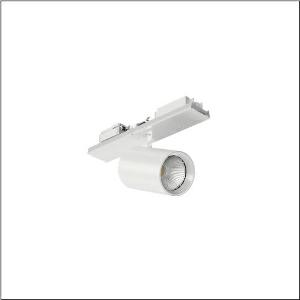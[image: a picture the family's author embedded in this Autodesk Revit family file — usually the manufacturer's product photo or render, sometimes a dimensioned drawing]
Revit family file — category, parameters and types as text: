
# Revit family: licross_r__spot_31_51sl13da45b_aeee
name_source: partatom
category: Lighting Fixtures
units: mm (PartAtom-declared; Revit-internal decimal feet)

## family parameters
Cut with Voids When Loaded = No
Host = Face
Light Source = No
Part Type = Normal
Room Calculation Point = No
Round Connector Dimension = Use Diameter
Shared = No

## types (1)
- --- (1 x LED, 5190 lm, 43.9 W, 4000K)
    Apparent Load = 44 VA
    CIE Flux Codes = 92 97 99 100 100
    Color Rendering = 90
    Color Temperature = 4000K
    Default Elevation = 1800 mm
    Description = Licross® Spot 31, directional spotlight, light control with lens, of plastic, LED rated luminous flux: 5.190lm, light colour: 940, with plug, 5-pole, mains connection: 220..240V, AC, 50/60Hz, of aluminium, traffic white (RAL 9016), length: 140mm, diameter: 90mm, protection rating (complete): IP20, insulation class (complete): insulation class I (protective earthing), certification: CE, packaging unit: 1 piece
    Height = 175 mm
    Lamp = 1 x LED
    Lamp Light Flux = 5190 lm
    Lamp Power = 43.9 W
    Lamp count = 1
    Length = 90 mm
    Luminous efficacy = 118 lm/W
    Manufacturer = Siteco
    ModVariant = No
    Model = 51SL13DA45B
    Mounting Place = Ceiling
    Mounting Type = Pendant
    Number of Poles = 1
    OnlyDefault = Yes
    Power Factor = 1
    Product Name = Licross® Spot 31
    Product group = directional spotlight
    ProductGroupID = 905
    Protection Class = Protection class I
    Protection Degree = IP 20
    RLX_Detail_Level = 1
    RLX_Emergency_Light_Flux = 0 lm
    RLX_Emergency_Type = 0
    RLX_Emergency_Type_DB = No
    RlxData = <blob elided: 14777 chars, md5=18c073ff>
    Socket = socket
    Standby Power = 0 W
    System Light Flux = 5190 lm
    System Power = 44 W
    Type Comments = factory setting: luminous flux: 100 % | (ON | ON | ON) | 1050 mA
    Type Image = l_1245720.jpg
    URL = http://relux.com
    VarID = @adj_081827
    Voltage = 0 V
    Weight = 0.00 kg
    Width = 0 mm  [stored 0 ft]

note: [stored X ft] marks values corroborated as IEEE doubles in the binary element streams (Revit-internal decimal feet)

## geometry (parser evidence)
native form markers: Sweep x11
no freeform markers — native parametric forms only
